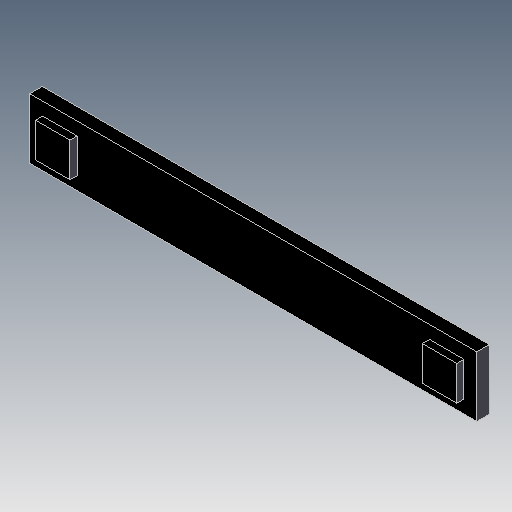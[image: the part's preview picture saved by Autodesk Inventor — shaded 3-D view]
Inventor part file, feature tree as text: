
AUTODESK INVENTOR PART (.ipt)
format: ipt  version: 2021 (Build 250183000, 183)  size: 152,576 bytes
history: native  units: mm
features: extrude x3, sketch x3
ambient origin geometry x8: Origin, YZ Plane, XZ Plane, XY Plane, X Axis, Y Axis, Z Axis, Center Point
bodies: Volumenkörper1 (feature_tree)
feature tree (6):
  extrude  "Extrusion1"  Depth=24.0mm
  extrude  "Extrusion2"  Depth=24.0mm
  extrude  "Extrusion3"  Depth=178.0mm
  sketch  "Skizze1"  dims[d0=178.0mm d1=24.0mm]
  sketch  "Skizze3"  dims[d2=24.0mm d3=24.0mm]
  sketch  "Skizze4"  dims[d4=5.0mm d5=0.0mm d10=178.0mm d11=24.0mm d12=24.0mm d13=24.0mm d14=13.7mm d15=13.7mm d16=2.85mm d17=0.0mm d18=178.0mm d19=24.0mm d20=24.0mm d21=24.0mm d22=14.0mm d23=14.0mm d24=3.0mm d25=0.0mm]
